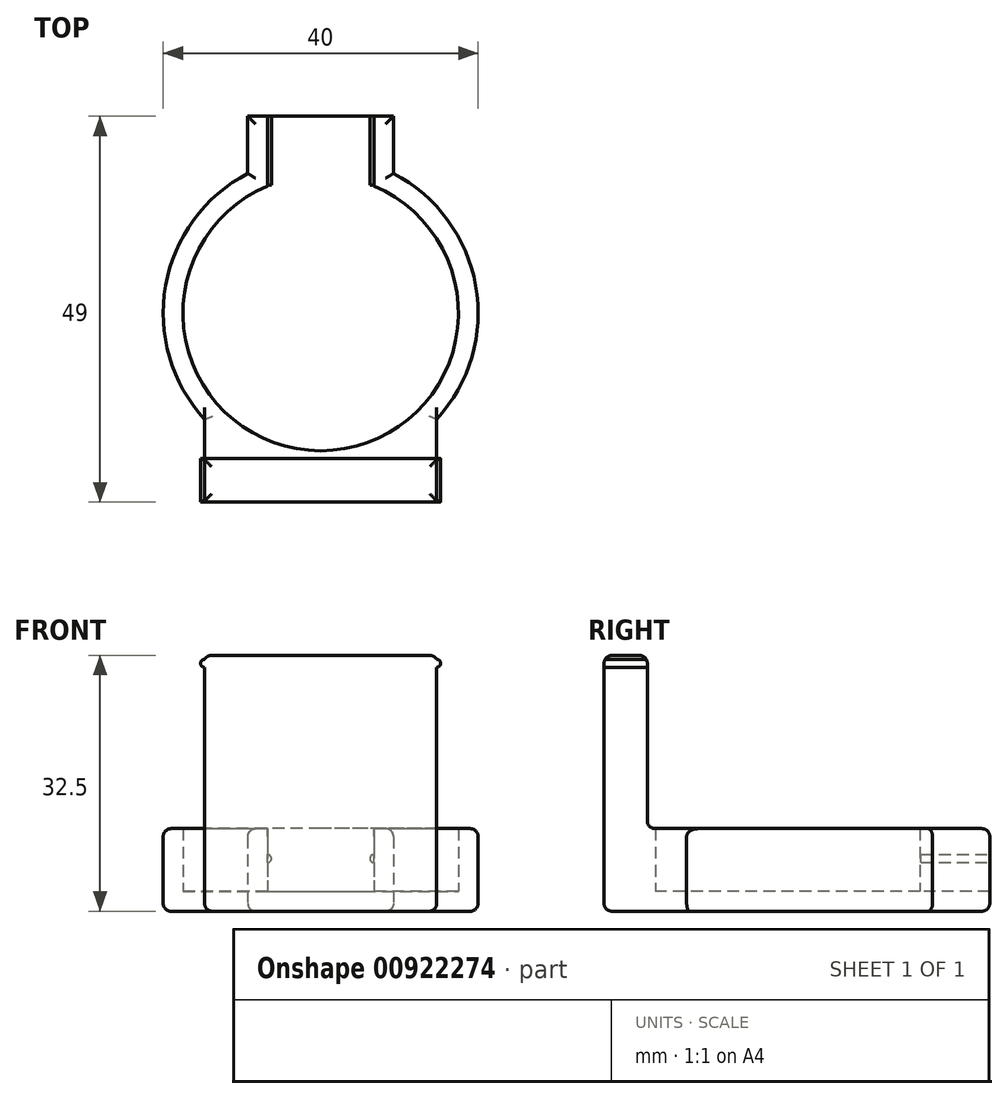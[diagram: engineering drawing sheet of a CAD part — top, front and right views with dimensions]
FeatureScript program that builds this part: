
annotation { "Feature Type Name" : "Feature", "Feature Type Description" : "" }
export const myFeature = defineFeature(function(context is Context, id is Id, definition is map)
    precondition{}
    {
        {
            var Q0;
            Q0=qCreatedBy(makeId("Top.planeOp"),FACE);
            var sketch = newSketch(context, id + "F0", { "sketchPlane" : qUnion([Q0])});
            skCircle(sketch, "E0", {"center": v(0, 0) * mm, "radius": 20 * mm});
            skLineSegment(sketch, "E1.bottom", {"start": v(-9.25, 25) * mm, "end": v(9.25, 25) * mm});
            skLineSegment(sketch, "E1.top", {"start": v(-9.25, 0) * mm, "end": v(9.25, 0) * mm});
            skLineSegment(sketch, "E1.left", {"start": v(-9.25, 25) * mm, "end": v(-9.25, 0) * mm});
            skLineSegment(sketch, "E1.right", {"start": v(9.25, 25) * mm, "end": v(9.25, 0) * mm});
            skLineSegment(sketch, "E2.bottom", {"start": v(-14.75, -12) * mm, "end": v(14.75, -12) * mm});
            skLineSegment(sketch, "E2.top", {"start": v(-14.75, -24) * mm, "end": v(14.75, -24) * mm});
            skLineSegment(sketch, "E2.left", {"start": v(-14.75, -12) * mm, "end": v(-14.75, -24) * mm});
            skLineSegment(sketch, "E2.right", {"start": v(14.75, -12) * mm, "end": v(14.75, -24) * mm});
            skSolve(sketch);
        }
        {
            var Q0;
            Q0 = qSketchRegion(id + "F0", true);
            extrude(context, id + "F1", {"entities" : qUnion([Q0]), "depth" : 30 * mm, "offsetDistance" : 25 * mm});
        }
        {
            var Q0;
            Q0=makeQuery(id+"F1.opExtrude","CAP_FACE",FACE,{"disambiguationData":[OSD([sQuery(id+"F0.wireOp",EDGE,"E0"),sQuery(id+"F0.wireOp",EDGE,"E1.bottom"),sQuery(id+"F0.wireOp",EDGE,"E1.left"),sQuery(id+"F0.wireOp",EDGE,"E1.right")])],"isStart":true});
            extrude(context, id + "F2", {"entities" : qUnion([Q0]), "operationType" : NewBodyOperationType.ADD, "depth" : 2.5 * mm, "offsetDistance" : 25 * mm});
        }
        {
            var Q0;
            Q0=qCreatedBy(makeId("Top.planeOp"),FACE);
            var sketch = newSketch(context, id + "F3", { "sketchPlane" : qUnion([Q0])});
            skCircle(sketch, "E3", {"center": v(0, 0) * mm, "radius": 17.5 * mm});
            skLineSegment(sketch, "E4.bottom", {"start": v(-6.75, 25) * mm, "end": v(6.75, 25) * mm});
            skLineSegment(sketch, "E4.top", {"start": v(-6.75, 0) * mm, "end": v(6.75, 0) * mm});
            skLineSegment(sketch, "E4.left", {"start": v(-6.75, 25) * mm, "end": v(-6.75, 0) * mm});
            skLineSegment(sketch, "E4.right", {"start": v(6.75, 25) * mm, "end": v(6.75, 0) * mm});
            skSolve(sketch);
        }
        {
            var Q0;
            Q0 = qSketchRegion(id + "F3", true);
            extrude(context, id + "F4", {"entities" : qUnion([Q0]), "operationType" : NewBodyOperationType.REMOVE, "depth" : 40 * mm, "offsetDistance" : 25 * mm});
        }
        {
            var Q0;
            Q0=qCreatedBy(makeId("Right.planeOp"),FACE);
            var sketch = newSketch(context, id + "F5", { "sketchPlane" : qUnion([Q0])});
            skLineSegment(sketch, "E5.bottom", {"start": v(31.5, 38) * mm, "end": v(-18.5, 38) * mm});
            skLineSegment(sketch, "E5.top", {"start": v(31.5, 8) * mm, "end": v(-18.5, 8) * mm});
            skLineSegment(sketch, "E5.left", {"start": v(31.5, 38) * mm, "end": v(31.5, 8) * mm});
            skLineSegment(sketch, "E5.right", {"start": v(-18.5, 38) * mm, "end": v(-18.5, 8) * mm});
            skSolve(sketch);
        }
        {
            var Q0;
            Q0=makeQuery(id+"F5.imprint","IMPRINT",FACE,{"disambiguationData":[TD([[makeQuery(id+"F5.imprint","IMPRINT",EDGE,{"derivedFrom":sQuery(id+"F5.wireOp",EDGE,"E5.bottom")}),1.0]])]});
            extrude(context, id + "F6", {"entities" : qUnion([Q0]), "operationType" : NewBodyOperationType.REMOVE, "endBound" : BoundingType.SYMMETRIC, "depth" : 50 * mm, "offsetDistance" : 25 * mm});
        }
        {
            var Q0;
            {var subQ0=sQuery(id+"F0.wireOp",EDGE,"E2.top");Q0=makeQuery(id+"F2.boolean.opBoolean","MERGE",FACE,{"derivedFrom":[makeQuery(id+"F1.opExtrude","SWEPT_FACE",FACE,{"disambiguationData":[OSD([subQ0])]}),makeQuery(id+"F2.opExtrude","SWEPT_FACE",FACE,{"disambiguationData":[OSD([subQ0])]})]});}
            var sketch = newSketch(context, id + "F7", { "sketchPlane" : qUnion([Q0])});
            skCircle(sketch, "E6", {"center": v(-14.75, 29) * mm, "radius": 0.5 * mm});
            skCircle(sketch, "E7", {"center": v(14.75, 29) * mm, "radius": 0.5 * mm});
            skSolve(sketch);
        }
        {
            var Q0;
            Q0 = qSketchRegion(id + "F7", true);
            extrude(context, id + "F8", {"entities" : qUnion([Q0]), "operationType" : NewBodyOperationType.ADD, "oppositeDirection" : true, "depth" : 5.5 * mm, "offsetDistance" : 25 * mm});
        }
        {
            var Q0;
            Q0=makeQuery(id+"F2.opExtrude","CAP_FACE",FACE,{"disambiguationData":[OSD([sQuery(id+"F0.wireOp",EDGE,"E0"),sQuery(id+"F0.wireOp",EDGE,"E1.bottom"),sQuery(id+"F0.wireOp",EDGE,"E1.left"),sQuery(id+"F0.wireOp",EDGE,"E1.right"),sQuery(id+"F0.wireOp",EDGE,"E2.top"),sQuery(id+"F0.wireOp",EDGE,"E2.left"),sQuery(id+"F0.wireOp",EDGE,"E2.right")])],"isStart":false});
            var Q1;
            Q1=makeQuery(id+"F1.opExtrude","CAP_FACE",FACE,{"disambiguationData":[OSD([sQuery(id+"F0.wireOp",EDGE,"E0"),sQuery(id+"F0.wireOp",EDGE,"E1.bottom"),sQuery(id+"F0.wireOp",EDGE,"E1.left"),sQuery(id+"F0.wireOp",EDGE,"E1.right"),sQuery(id+"F0.wireOp",EDGE,"E2.top"),sQuery(id+"F0.wireOp",EDGE,"E2.left"),sQuery(id+"F0.wireOp",EDGE,"E2.right")])],"isStart":false});
            var Q2;
            Q2=makeQuery(id+"F6.boolean.opBoolean","COPY",EDGE,{"derivedFrom":makeQuery(id+"F6.opExtrude","SWEPT_EDGE",EDGE,{"disambiguationData":[OSD([sQuery(id+"F5.wireOp",EDGE,"E5.top"),sQuery(id+"F5.wireOp",EDGE,"E5.right")])]})});
            var Q3;
            {var subQ0=sQuery(id+"F0.wireOp",EDGE,"E1.bottom");Q3=makeQuery(id+"F6.boolean.opBoolean","INTERSECT",EDGE,{"disambiguationData":[OD(0.0)],"derivedFrom":[makeQuery(id+"F2.boolean.opBoolean","MERGE",FACE,{"derivedFrom":[makeQuery(id+"F1.opExtrude","SWEPT_FACE",FACE,{"disambiguationData":[OSD([subQ0])]}),makeQuery(id+"F2.opExtrude","SWEPT_FACE",FACE,{"disambiguationData":[OSD([subQ0])]})]}),makeQuery(id+"F6.opExtrude","SWEPT_FACE",FACE,{"disambiguationData":[OSD([sQuery(id+"F5.wireOp",EDGE,"E5.top")])]})]});}
            var Q4;
            {var subQ0=sQuery(id+"F0.wireOp",EDGE,"E1.bottom");Q4=makeQuery(id+"F6.boolean.opBoolean","INTERSECT",EDGE,{"disambiguationData":[OD(1.0)],"derivedFrom":[makeQuery(id+"F2.boolean.opBoolean","MERGE",FACE,{"derivedFrom":[makeQuery(id+"F1.opExtrude","SWEPT_FACE",FACE,{"disambiguationData":[OSD([subQ0])]}),makeQuery(id+"F2.opExtrude","SWEPT_FACE",FACE,{"disambiguationData":[OSD([subQ0])]})]}),makeQuery(id+"F6.opExtrude","SWEPT_FACE",FACE,{"disambiguationData":[OSD([sQuery(id+"F5.wireOp",EDGE,"E5.top")])]})]});}
            var Q5;
            {var subQ0=sQuery(id+"F0.wireOp",EDGE,"E1.right");Q5=makeQuery(id+"F6.boolean.opBoolean","INTERSECT",EDGE,{"derivedFrom":[makeQuery(id+"F2.boolean.opBoolean","MERGE",FACE,{"derivedFrom":[makeQuery(id+"F1.opExtrude","SWEPT_FACE",FACE,{"disambiguationData":[OSD([subQ0])]}),makeQuery(id+"F2.opExtrude","SWEPT_FACE",FACE,{"disambiguationData":[OSD([subQ0])]})]}),makeQuery(id+"F6.opExtrude","SWEPT_FACE",FACE,{"disambiguationData":[OSD([sQuery(id+"F5.wireOp",EDGE,"E5.top")])]})]});}
            var Q6;
            {var subQ0=sQuery(id+"F0.wireOp",EDGE,"E0");var subQ1=makeQuery(id+"F0.imprint","IMPRINT",EDGE,{"disambiguationData":[TD([[makeQuery(id+"F0.imprint","INTERSECT",VERTEX,{"derivedFrom":[subQ0,sQuery(id+"F0.wireOp",EDGE,"E1.right")]}),1.0]])],"derivedFrom":subQ0});Q6=makeQuery(id+"F6.boolean.opBoolean","INTERSECT",EDGE,{"derivedFrom":[makeQuery(id+"F2.boolean.opBoolean","MERGE",FACE,{"derivedFrom":[makeQuery(id+"F1.opExtrude","SWEPT_FACE",FACE,{"disambiguationData":[OSD([subQ0]),TDD([subQ1])]}),makeQuery(id+"F2.opExtrude","SWEPT_FACE",FACE,{"disambiguationData":[OSD([subQ0]),TDD([makeQuery(id+"F1.opExtrude","CAP_EDGE",EDGE,{"disambiguationData":[OSD([subQ0]),TDD([subQ1])],"isStart":true})])]})]}),makeQuery(id+"F6.opExtrude","SWEPT_FACE",FACE,{"disambiguationData":[OSD([sQuery(id+"F5.wireOp",EDGE,"E5.top")])]})]});}
            var Q7;
            {var subQ0=sQuery(id+"F0.wireOp",EDGE,"E1.left");Q7=makeQuery(id+"F6.boolean.opBoolean","INTERSECT",EDGE,{"derivedFrom":[makeQuery(id+"F2.boolean.opBoolean","MERGE",FACE,{"derivedFrom":[makeQuery(id+"F1.opExtrude","SWEPT_FACE",FACE,{"disambiguationData":[OSD([subQ0])]}),makeQuery(id+"F2.opExtrude","SWEPT_FACE",FACE,{"disambiguationData":[OSD([subQ0])]})]}),makeQuery(id+"F6.opExtrude","SWEPT_FACE",FACE,{"disambiguationData":[OSD([sQuery(id+"F5.wireOp",EDGE,"E5.top")])]})]});}
            var Q8;
            {var subQ0=sQuery(id+"F0.wireOp",EDGE,"E0");var subQ1=makeQuery(id+"F0.imprint","IMPRINT",EDGE,{"disambiguationData":[TD([[makeQuery(id+"F0.imprint","INTERSECT",VERTEX,{"derivedFrom":[subQ0,sQuery(id+"F0.wireOp",EDGE,"E1.left")]}),-1.0]])],"derivedFrom":subQ0});Q8=makeQuery(id+"F6.boolean.opBoolean","INTERSECT",EDGE,{"derivedFrom":[makeQuery(id+"F2.boolean.opBoolean","MERGE",FACE,{"derivedFrom":[makeQuery(id+"F1.opExtrude","SWEPT_FACE",FACE,{"disambiguationData":[OSD([subQ0]),TDD([subQ1])]}),makeQuery(id+"F2.opExtrude","SWEPT_FACE",FACE,{"disambiguationData":[OSD([subQ0]),TDD([makeQuery(id+"F1.opExtrude","CAP_EDGE",EDGE,{"disambiguationData":[OSD([subQ0]),TDD([subQ1])],"isStart":true})])]})]}),makeQuery(id+"F6.opExtrude","SWEPT_FACE",FACE,{"disambiguationData":[OSD([sQuery(id+"F5.wireOp",EDGE,"E5.top")])]})]});}
            fillet(context, id + "F9", {"entities" : qUnion([Q0, Q1, Q2, Q3, Q4, Q5, Q6, Q7, Q8]), "radius" : 1 * mm, "tangentPropagation" : true, "allowEdgeOverflow" : false});
        }
        {
            var Q0;
            {var subQ0=sQuery(id+"F0.wireOp",EDGE,"E1.bottom");Q0=makeQuery(id+"F2.boolean.opBoolean","MERGE",FACE,{"derivedFrom":[makeQuery(id+"F1.opExtrude","SWEPT_FACE",FACE,{"disambiguationData":[OSD([subQ0])]}),makeQuery(id+"F2.opExtrude","SWEPT_FACE",FACE,{"disambiguationData":[OSD([subQ0])]})]});}
            var sketch = newSketch(context, id + "F10", { "sketchPlane" : qUnion([Q0])});
            skCircle(sketch, "E8", {"center": v(-6.75, 4.2) * mm, "radius": 0.5 * mm});
            skCircle(sketch, "E9", {"center": v(6.75, 4.2) * mm, "radius": 0.5 * mm});
            skSolve(sketch);
        }
        {
            var Q0;
            Q0 = qSketchRegion(id + "F10", true);
            extrude(context, id + "F11", {"entities" : qUnion([Q0]), "operationType" : NewBodyOperationType.ADD, "oppositeDirection" : true, "depth" : 8.75 * mm, "offsetDistance" : 25 * mm});
        }
    });
